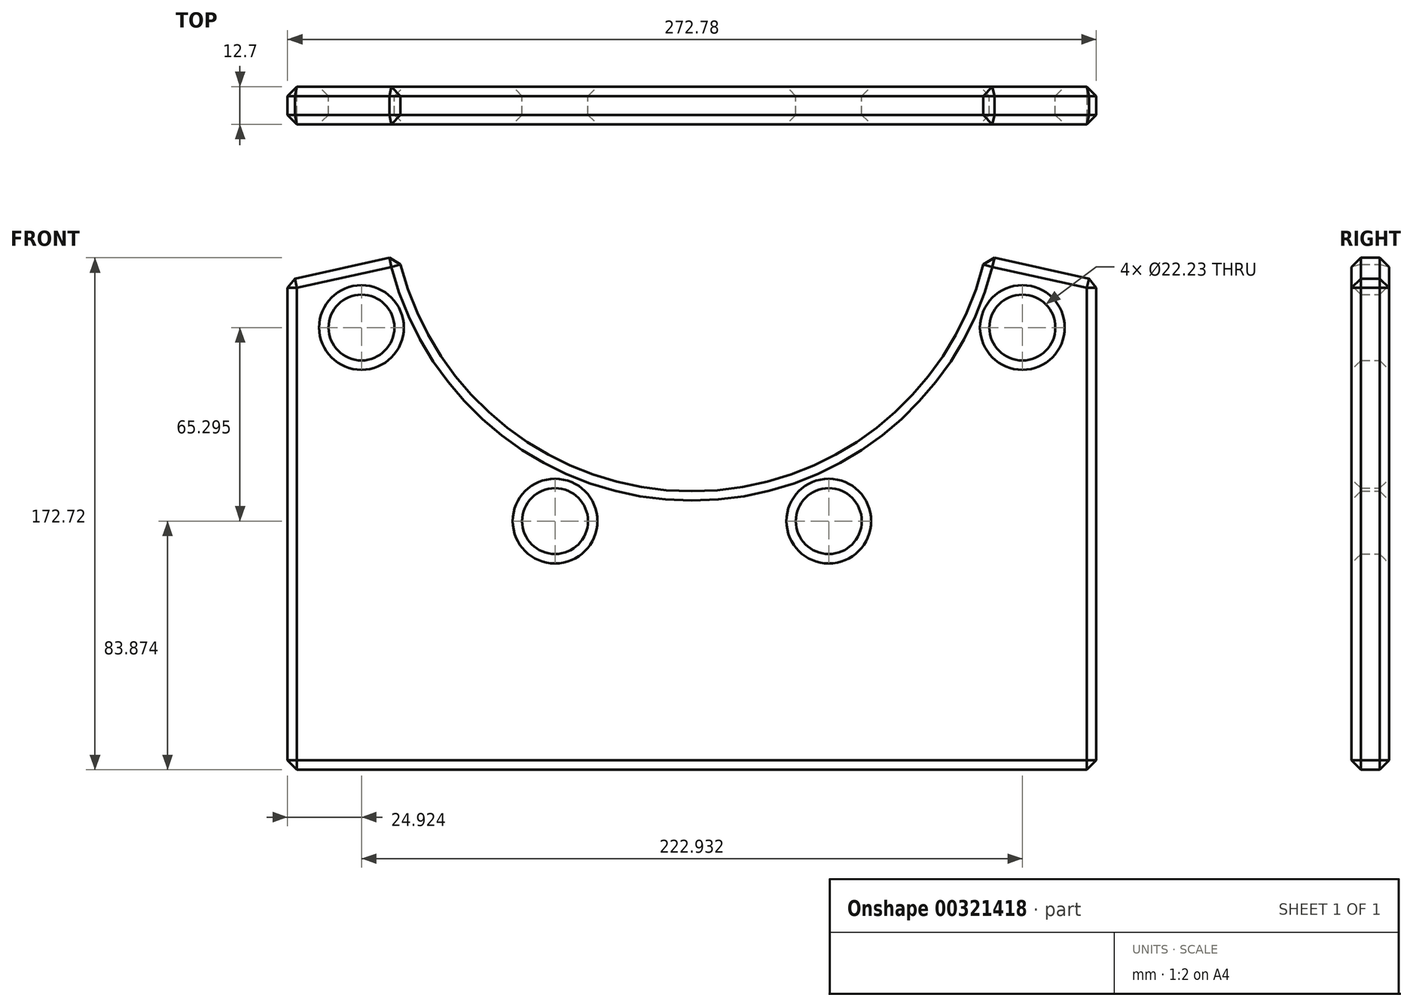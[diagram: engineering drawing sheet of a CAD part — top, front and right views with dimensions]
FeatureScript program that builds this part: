
annotation { "Feature Type Name" : "Feature", "Feature Type Description" : "" }
export const myFeature = defineFeature(function(context is Context, id is Id, definition is map)
    precondition{}
    {
        {
            var Q0;
            Q0=qCreatedBy(makeId("Front.planeOp"),FACE);
            var sketch = newSketch(context, id + "F0", { "sketchPlane" : qUnion([Q0])});
            skArc(sketch, "E0", {"start": v(-117.8, -26.11) * mm, "mid": v(0, -120.65) * mm, "end": v(117.8, -26.11) * mm});
            skCircle(sketch, "E1", {"center": v(-46.17, -111.47) * mm, "radius": 11.11 * mm});
            skCircle(sketch, "E2.1.0", {"center": v(46.17, -111.47) * mm, "radius": 11.11 * mm});
            skCircle(sketch, "E2.2.0", {"center": v(111.47, -46.17) * mm, "radius": 11.11 * mm});
            skCircle(sketch, "E3.1.7.0", {"center": v(-111.47, -46.17) * mm, "radius": 11.11 * mm});
            skArc(sketch, "E4", {"start": v(-99, -21.95) * mm, "mid": v(0, -101.4) * mm, "end": v(99, -21.95) * mm});
            skArc(sketch, "E5", {"start": v(-136.39, -30.24) * mm, "mid": v(0, -139.7) * mm, "end": v(136.39, -30.24) * mm});
            skLineSegment(sketch, "E6", {"start": v(99, -21.95) * mm, "end": v(136.39, -30.24) * mm});
            skLineSegment(sketch, "E7.trimOffspring", {"start": v(-99, -21.95) * mm, "end": v(-136.39, -30.24) * mm});
            skLineSegment(sketch, "E8", {"start": v(-136.39, -30.24) * mm, "end": v(-136.39, -195.34) * mm});
            skLineSegment(sketch, "E9", {"start": v(-136.39, -195.34) * mm, "end": v(136.39, -195.34) * mm});
            skLineSegment(sketch, "E10", {"start": v(136.39, -195.34) * mm, "end": v(136.39, -30.24) * mm});
            skSolve(sketch);
        }
        {
            var Q0;
            Q0=makeQuery(id+"F0.imprint","IMPRINT",FACE,{"disambiguationData":[TD([[makeQuery(id+"F0.imprint","IMPRINT",EDGE,{"derivedFrom":sQuery(id+"F0.wireOp",EDGE,"E5")}),-1.0]])]});
            var Q1;
            {var subQ0=sQuery(id+"F0.wireOp",EDGE,"E5");Q1=makeQuery(id+"F0.imprint","IMPRINT",FACE,{"disambiguationData":[TD([[makeQuery(id+"F0.imprint","IMPRINT",EDGE,{"derivedFrom":subQ0}),1.0]])]});}
            var Q2;
            {var subQ17=sQuery(id+"F0.wireOp",EDGE,"E4");Q2=makeQuery(id+"F0.imprint","IMPRINT",FACE,{"disambiguationData":[TD([[makeQuery(id+"F0.imprint","IMPRINT",EDGE,{"derivedFrom":subQ17}),-1.0]])]});}
            extrude(context, id + "F1", {"entities" : qUnion([Q0, Q1, Q2]), "endBound" : BoundingType.SYMMETRIC, "depth" : 12.7 * mm});
        }
        {
            var Q0;
            Q0=makeQuery(id+"F1.opExtrude","CAP_FACE",FACE,{"disambiguationData":[OSD([sQuery(id+"F0.wireOp",EDGE,"E1"),sQuery(id+"F0.wireOp",EDGE,"E2.1.0"),sQuery(id+"F0.wireOp",EDGE,"E2.2.0"),sQuery(id+"F0.wireOp",EDGE,"E3.1.7.0"),sQuery(id+"F0.wireOp",EDGE,"E4"),sQuery(id+"F0.wireOp",EDGE,"E6"),sQuery(id+"F0.wireOp",EDGE,"E7.trimOffspring"),sQuery(id+"F0.wireOp",EDGE,"E8"),sQuery(id+"F0.wireOp",EDGE,"E9"),sQuery(id+"F0.wireOp",EDGE,"E10")])],"isStart":false});
            var Q1;
            Q1=makeQuery(id+"F1.opExtrude","CAP_FACE",FACE,{"disambiguationData":[OSD([sQuery(id+"F0.wireOp",EDGE,"E1"),sQuery(id+"F0.wireOp",EDGE,"E2.1.0"),sQuery(id+"F0.wireOp",EDGE,"E2.2.0"),sQuery(id+"F0.wireOp",EDGE,"E3.1.7.0"),sQuery(id+"F0.wireOp",EDGE,"E4"),sQuery(id+"F0.wireOp",EDGE,"E6"),sQuery(id+"F0.wireOp",EDGE,"E7.trimOffspring"),sQuery(id+"F0.wireOp",EDGE,"E8"),sQuery(id+"F0.wireOp",EDGE,"E9"),sQuery(id+"F0.wireOp",EDGE,"E10")])],"isStart":true});
            var Q2;
            Q2=makeQuery(id+"F1.opExtrude","SWEPT_EDGE",EDGE,{"disambiguationData":[OSD([sQuery(id+"F0.wireOp",EDGE,"E5"),sQuery(id+"F0.wireOp",EDGE,"E7.trimOffspring"),sQuery(id+"F0.wireOp",EDGE,"E8")])]});
            var Q3;
            Q3=makeQuery(id+"F1.opExtrude","SWEPT_EDGE",EDGE,{"disambiguationData":[OSD([sQuery(id+"F0.wireOp",EDGE,"E4"),sQuery(id+"F0.wireOp",EDGE,"E7.trimOffspring")])]});
            var Q4;
            Q4=makeQuery(id+"F1.opExtrude","SWEPT_EDGE",EDGE,{"disambiguationData":[OSD([sQuery(id+"F0.wireOp",EDGE,"E4"),sQuery(id+"F0.wireOp",EDGE,"E6")])]});
            var Q5;
            Q5=makeQuery(id+"F1.opExtrude","SWEPT_EDGE",EDGE,{"disambiguationData":[OSD([sQuery(id+"F0.wireOp",EDGE,"E5"),sQuery(id+"F0.wireOp",EDGE,"E6"),sQuery(id+"F0.wireOp",EDGE,"E10")])]});
            var Q6;
            Q6=makeQuery(id+"F1.opExtrude","SWEPT_EDGE",EDGE,{"disambiguationData":[OSD([sQuery(id+"F0.wireOp",EDGE,"E9"),sQuery(id+"F0.wireOp",EDGE,"E10")])]});
            var Q7;
            Q7=makeQuery(id+"F1.opExtrude","SWEPT_EDGE",EDGE,{"disambiguationData":[OSD([sQuery(id+"F0.wireOp",EDGE,"E8"),sQuery(id+"F0.wireOp",EDGE,"E9")])]});
            chamfer(context, id + "F2", {"entities" : qUnion([Q0, Q1, Q2, Q3, Q4, Q5, Q6, Q7]), "width" : 3.17 * mm, "tangentPropagation" : true});
        }
    });
